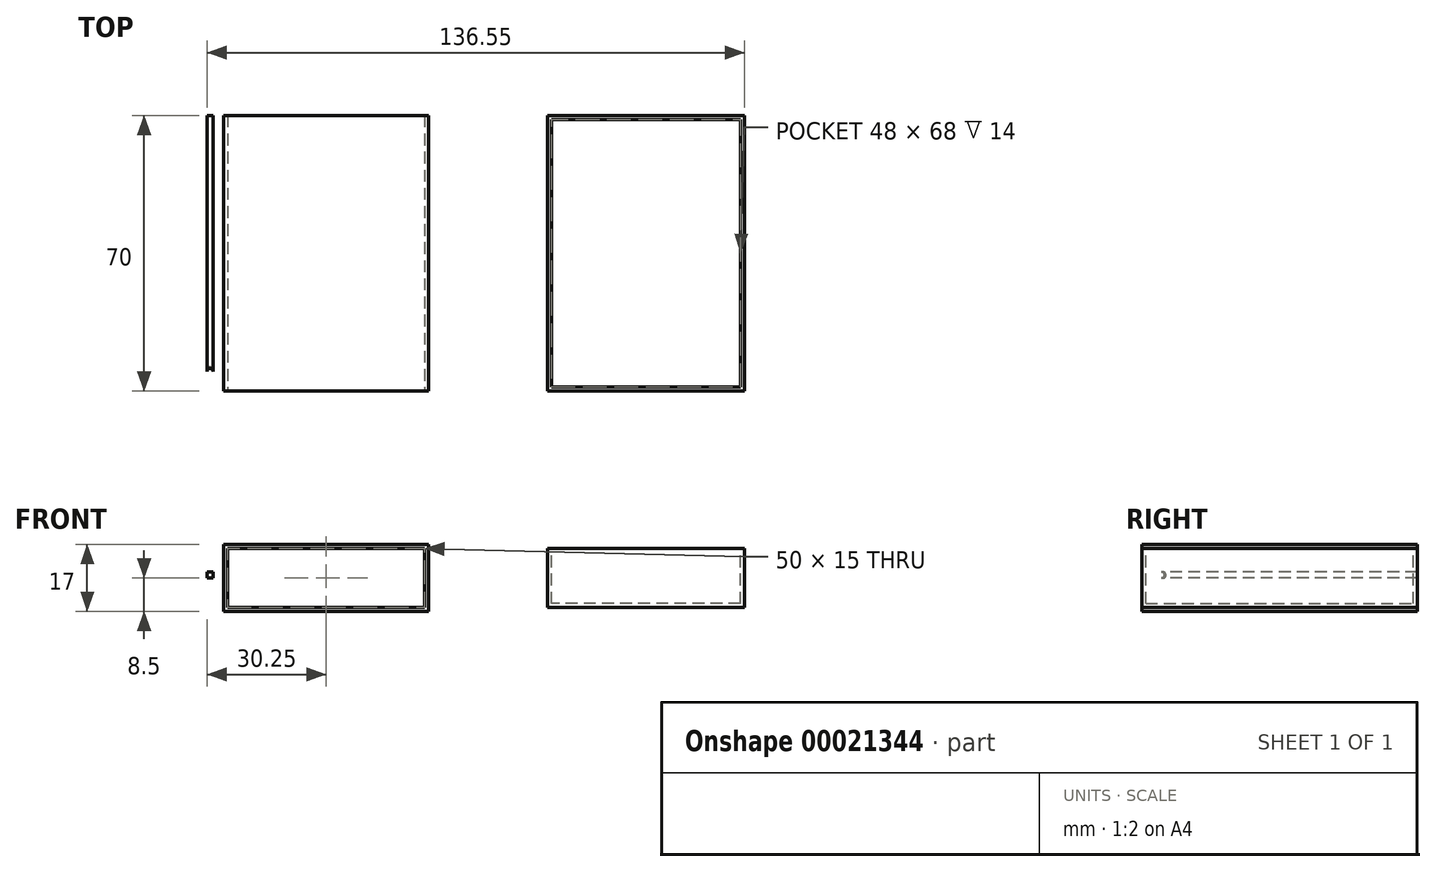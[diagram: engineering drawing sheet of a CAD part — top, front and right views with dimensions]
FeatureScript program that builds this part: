
annotation { "Feature Type Name" : "Feature", "Feature Type Description" : "" }
export const myFeature = defineFeature(function(context is Context, id is Id, definition is map)
    precondition{}
    {
        {
            var Q0;
            Q0=qCreatedBy(makeId("Front.planeOp"),FACE);
            var sketch = newSketch(context, id + "F0", { "sketchPlane" : qUnion([Q0])});
            skLineSegment(sketch, "E0.rect.bottom", {"start": v(-26, 8.5) * mm, "end": v(26, 8.5) * mm});
            skLineSegment(sketch, "E0.rect.top", {"start": v(-26, -8.5) * mm, "end": v(26, -8.5) * mm});
            skLineSegment(sketch, "E0.rect.left", {"start": v(-26, 8.5) * mm, "end": v(-26, -8.5) * mm});
            skLineSegment(sketch, "E0.rect.right", {"start": v(26, 8.5) * mm, "end": v(26, -8.5) * mm});
            skPoint(sketch, "E0.rect.middle", {"position": v(0, 0) * mm});
            skSolve(sketch);
        }
        {
            var Q0;
            Q0 = qSketchRegion(id + "F0", true);
            extrude(context, id + "F1", {"entities" : qUnion([Q0]), "depth" : 70 * mm});
        }
        {
            var Q0;
            Q0=makeQuery(id+"F1.opExtrude","CAP_FACE",FACE,{"disambiguationData":[OSD([sQuery(id+"F0.wireOp",EDGE,"E0.rect.bottom"),sQuery(id+"F0.wireOp",EDGE,"E0.rect.top"),sQuery(id+"F0.wireOp",EDGE,"E0.rect.left"),sQuery(id+"F0.wireOp",EDGE,"E0.rect.right")])],"isStart":false});
            var sketch = newSketch(context, id + "F2", { "sketchPlane" : qUnion([Q0])});
            skLineSegment(sketch, "E1.rect.bottom", {"start": v(-25, 7.5) * mm, "end": v(25, 7.5) * mm});
            skLineSegment(sketch, "E1.rect.top", {"start": v(-25, -7.5) * mm, "end": v(25, -7.5) * mm});
            skLineSegment(sketch, "E1.rect.left", {"start": v(-25, 7.5) * mm, "end": v(-25, -7.5) * mm});
            skLineSegment(sketch, "E1.rect.right", {"start": v(25, 7.5) * mm, "end": v(25, -7.5) * mm});
            skPoint(sketch, "E1.rect.middle", {"position": v(0, 0) * mm});
            skSolve(sketch);
        }
        {
            var Q0;
            Q0 = qSketchRegion(id + "F2", true);
            extrude(context, id + "F3", {"entities" : qUnion([Q0]), "operationType" : NewBodyOperationType.REMOVE, "endBound" : BoundingType.THROUGH_ALL, "oppositeDirection" : true, "depth" : 25 * mm});
        }
        {
            var Q0;
            Q0=qCreatedBy(makeId("Front.planeOp"),FACE);
            var sketch = newSketch(context, id + "F4", { "sketchPlane" : qUnion([Q0])});
            skLineSegment(sketch, "E2.rect.bottom", {"start": v(56.3, 7.5) * mm, "end": v(106.3, 7.5) * mm});
            skLineSegment(sketch, "E2.rect.top", {"start": v(56.3, -7.5) * mm, "end": v(106.3, -7.5) * mm});
            skLineSegment(sketch, "E2.rect.left", {"start": v(56.3, 7.5) * mm, "end": v(56.3, -7.5) * mm});
            skLineSegment(sketch, "E2.rect.right", {"start": v(106.3, 7.5) * mm, "end": v(106.3, -7.5) * mm});
            skPoint(sketch, "E2.rect.middle", {"position": v(81.3, 0) * mm});
            skSolve(sketch);
        }
        {
            var Q0;
            Q0 = qSketchRegion(id + "F4", true);
            extrude(context, id + "F5", {"entities" : qUnion([Q0]), "depth" : 70 * mm});
        }
        {
            var Q0;
            Q0=makeQuery(id+"F5.opExtrude","SWEPT_FACE",FACE,{"disambiguationData":[OSD([sQuery(id+"F4.wireOp",EDGE,"E2.rect.bottom")])]});
            var sketch = newSketch(context, id + "F6", { "sketchPlane" : qUnion([Q0])});
            skLineSegment(sketch, "E3.rect.bottom", {"start": v(105.3, -69) * mm, "end": v(57.3, -69) * mm});
            skLineSegment(sketch, "E3.rect.top", {"start": v(105.3, -1) * mm, "end": v(57.3, -1) * mm});
            skLineSegment(sketch, "E3.rect.left", {"start": v(105.3, -69) * mm, "end": v(105.3, -1) * mm});
            skLineSegment(sketch, "E3.rect.right", {"start": v(57.3, -69) * mm, "end": v(57.3, -1) * mm});
            skPoint(sketch, "E3.rect.middle", {"position": v(81.3, -35) * mm});
            skLineSegment(sketch, "E4", {"start": v(81.3, 0) * mm, "end": v(81.3, -70) * mm, "construction": true});
            skSolve(sketch);
        }
        {
            var Q0;
            Q0 = qSketchRegion(id + "F6", true);
            extrude(context, id + "F7", {"entities" : qUnion([Q0]), "operationType" : NewBodyOperationType.REMOVE, "oppositeDirection" : true, "depth" : 14 * mm});
        }
        {
            var Q0;
            Q0=qCreatedBy(makeId("Top.planeOp"),FACE);
            var sketch = newSketch(context, id + "F8", { "sketchPlane" : qUnion([Q0])});
            skLineSegment(sketch, "E5.bottom", {"start": v(-30.25, 0) * mm, "end": v(-28.75, 0) * mm});
            skLineSegment(sketch, "E5.top", {"start": v(-30.25, -65) * mm, "end": v(-28.75, -65) * mm});
            skLineSegment(sketch, "E5.left", {"start": v(-30.25, 0) * mm, "end": v(-30.25, -65) * mm});
            skLineSegment(sketch, "E5.right", {"start": v(-28.75, 0) * mm, "end": v(-28.75, -65) * mm});
            skSolve(sketch);
        }
        {
            var Q0;
            Q0 = qSketchRegion(id + "F8", true);
            extrude(context, id + "F9", {"entities" : qUnion([Q0]), "depth" : 1.5 * mm});
        }
        {
            var Q0;
            Q0=makeQuery(id+"F9.opExtrude","SWEPT_FACE",FACE,{"disambiguationData":[OSD([sQuery(id+"F8.wireOp",EDGE,"E5.top")])]});
            var sketch = newSketch(context, id + "F10", { "sketchPlane" : qUnion([Q0])});
            skArc(sketch, "E6", {"start": v(-28.75, 1.5) * mm, "mid": v(-30.25, 1.5) * mm, "end": v(-30.25, 0) * mm});
            skLineSegment(sketch, "E7", {"start": v(-30.25, 0) * mm, "end": v(-28.75, 1.5) * mm});
            skSolve(sketch);
        }
        {
            var Q0;
            Q0 = qSketchRegion(id + "F10", true);
            var Q1;
            Q1=sQuery(id+"F10.wireOp",EDGE,"E7");
            revolve(context, id + "F11", {"operationType" : NewBodyOperationType.ADD, "entities" : qUnion([Q0]), "axis" : qUnion([Q1]), "revolveType" : RevolveType.FULL});
        }
    });
